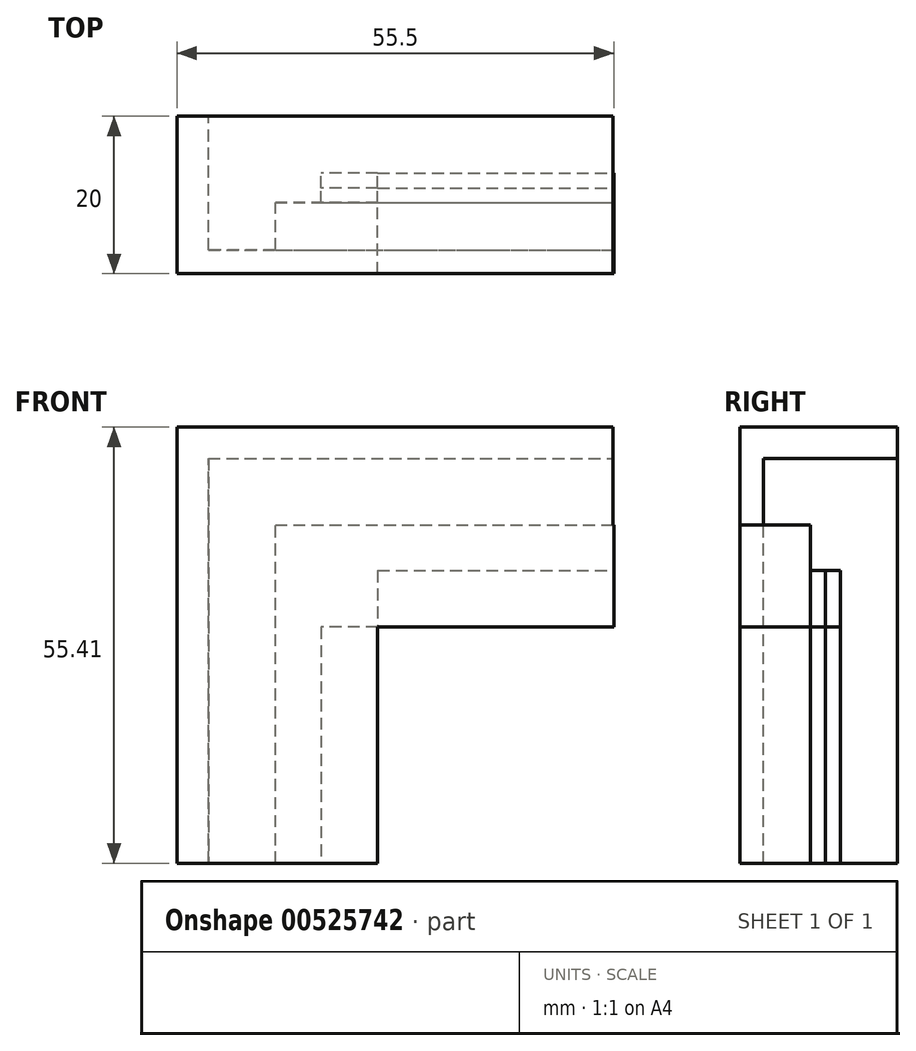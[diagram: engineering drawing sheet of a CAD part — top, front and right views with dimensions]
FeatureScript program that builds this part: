
annotation { "Feature Type Name" : "Feature", "Feature Type Description" : "" }
export const myFeature = defineFeature(function(context is Context, id is Id, definition is map)
    precondition{}
    {
        {
            var Q0;
            Q0=qCreatedBy(makeId("Front.planeOp"),FACE);
            var sketch = newSketch(context, id + "F0", { "sketchPlane" : qUnion([Q0])});
            skLineSegment(sketch, "E0.bottom", {"start": v(0, 0) * mm, "end": v(-7.2, 0) * mm});
            skLineSegment(sketch, "E0.top", {"start": v(0, -30) * mm, "end": v(-7.2, -30) * mm});
            skLineSegment(sketch, "E0.left", {"start": v(0, 0) * mm, "end": v(0, -30) * mm});
            skLineSegment(sketch, "E0.right", {"start": v(-7.2, 0) * mm, "end": v(-7.2, -30) * mm});
            skLineSegment(sketch, "E1.bottom", {"start": v(0, 0) * mm, "end": v(30, 0) * mm});
            skLineSegment(sketch, "E1.top", {"start": v(0, 7.2) * mm, "end": v(30, 7.2) * mm});
            skLineSegment(sketch, "E1.left", {"start": v(0, 0) * mm, "end": v(0, 7.2) * mm});
            skLineSegment(sketch, "E1.right", {"start": v(30, 0) * mm, "end": v(30, 7.2) * mm});
            skSolve(sketch);
        }
        {
            var Q0;
            Q0 = qSketchRegion(id + "F0", true);
            extrude(context, id + "F1", {"entities" : qUnion([Q0]), "depth" : 1.9 * mm, "offsetDistance" : 25 * mm});
        }
        {
            var Q0;
            Q0=qCreatedBy(makeId("Front.planeOp"),FACE);
            cPlane(context, id + "F2", {"entities" : qUnion([Q0]), "cplaneType" : CPlaneType.OFFSET, "offset" : 1.9 * mm, "width" : 150 * mm, "height" : 150 * mm});
        }
        {
            var Q0;
            Q0=qCreatedBy(id+"F2.planeOp",FACE);
            var sketch = newSketch(context, id + "F3", { "sketchPlane" : qUnion([Q0])});
            skLineSegment(sketch, "E2.bottom", {"start": v(0, -30) * mm, "end": v(-7.2, -30) * mm});
            skLineSegment(sketch, "E3.top", {"start": v(-7.2, 0) * mm, "end": v(30, 0) * mm});
            skLineSegment(sketch, "E3.right", {"start": v(30, 7.2) * mm, "end": v(30, 0) * mm});
            skLineSegment(sketch, "E4.top", {"start": v(-7.2, 0) * mm, "end": v(0, 0) * mm});
            skLineSegment(sketch, "E5.top", {"start": v(-7.2, -30) * mm, "end": v(0, -30) * mm});
            skLineSegment(sketch, "E5.left", {"start": v(-7.2, 0) * mm, "end": v(-7.2, -30) * mm});
            skLineSegment(sketch, "E5.right", {"start": v(0, 0) * mm, "end": v(0, -30) * mm});
            skLineSegment(sketch, "E6.bottom", {"start": v(0, 7.2) * mm, "end": v(30, 7.2) * mm});
            skLineSegment(sketch, "E6.top", {"start": v(0, 0) * mm, "end": v(30, 0) * mm});
            skLineSegment(sketch, "E6.left", {"start": v(0, 7.2) * mm, "end": v(0, 0) * mm});
            skSolve(sketch);
        }
        {
            var Q0;
            Q0=qCreatedBy(id+"F2.planeOp",FACE);
            cPlane(context, id + "F4", {"entities" : qUnion([Q0]), "cplaneType" : CPlaneType.OFFSET, "offset" : 1.9 * mm, "width" : 150 * mm, "height" : 150 * mm});
        }
        {
            var Q0;
            Q0=qCreatedBy(id+"F4.planeOp",FACE);
            var sketch = newSketch(context, id + "F5", { "sketchPlane" : qUnion([Q0])});
            skLineSegment(sketch, "E7.top", {"start": v(17.1, 0) * mm, "end": v(-12.9, 0) * mm});
            skLineSegment(sketch, "E8.bottom", {"start": v(0, -30) * mm, "end": v(-13, -30) * mm});
            skLineSegment(sketch, "E8.top", {"start": v(0, 13) * mm, "end": v(-13, 13) * mm});
            skLineSegment(sketch, "E8.left", {"start": v(0, -30) * mm, "end": v(0, 13) * mm});
            skLineSegment(sketch, "E8.right", {"start": v(-13, -30) * mm, "end": v(-13, 13) * mm});
            skLineSegment(sketch, "E9.bottom", {"start": v(-13, 13) * mm, "end": v(30, 13) * mm});
            skLineSegment(sketch, "E9.top", {"start": v(-13, 0) * mm, "end": v(30, 0) * mm});
            skLineSegment(sketch, "E9.left", {"start": v(-13, 13) * mm, "end": v(-13, 0) * mm});
            skLineSegment(sketch, "E9.right", {"start": v(30, 13) * mm, "end": v(30, 0) * mm});
            skSolve(sketch);
        }
        {
            var Q0;
            Q0 = qSketchRegion(id + "F5", true);
            extrude(context, id + "F6", {"entities" : qUnion([Q0]), "depth" : 9 * mm, "offsetDistance" : 25 * mm});
        }
        {
            var Q0;
            Q0 = qSketchRegion(id + "F3", true);
            extrude(context, id + "F7", {"entities" : qUnion([Q0]), "depth" : 1.9 * mm, "offsetDistance" : 25 * mm});
        }
        {
            var Q0;
            Q0=makeQuery(id+"F6.opExtrude","CAP_FACE",FACE,{"disambiguationData":[OSD([sQuery(id+"F5.wireOp",EDGE,"E8.bottom"),sQuery(id+"F5.wireOp",EDGE,"E8.left"),sQuery(id+"F5.wireOp",EDGE,"E8.right"),sQuery(id+"F5.wireOp",EDGE,"E9.bottom"),sQuery(id+"F5.wireOp",EDGE,"E9.top"),sQuery(id+"F5.wireOp",EDGE,"E9.left"),sQuery(id+"F5.wireOp",EDGE,"E9.right")])],"isStart":false});
            cPlane(context, id + "F8", {"entities" : qUnion([Q0]), "cplaneType" : CPlaneType.OFFSET, "offset" : 3 * mm, "oppositeDirection" : true, "width" : 150 * mm, "height" : 150 * mm});
        }
        {
            var Q0;
            Q0=qCreatedBy(id+"F8.planeOp",FACE);
            var sketch = newSketch(context, id + "F9", { "sketchPlane" : qUnion([Q0])});
            skLineSegment(sketch, "E10.bottom", {"start": v(-13, -30) * mm, "end": v(-21.5, -30) * mm});
            skLineSegment(sketch, "E10.top", {"start": v(-13, 12.9) * mm, "end": v(-21.5, 12.9) * mm});
            skLineSegment(sketch, "E10.left", {"start": v(-13, -30) * mm, "end": v(-13, 12.9) * mm});
            skLineSegment(sketch, "E10.right", {"start": v(-21.5, -30) * mm, "end": v(-21.5, 12.9) * mm});
            skLineSegment(sketch, "E11.bottom", {"start": v(-21.5, 12.9) * mm, "end": v(29.9, 12.9) * mm});
            skLineSegment(sketch, "E11.top", {"start": v(-21.5, 21.4) * mm, "end": v(29.9, 21.4) * mm});
            skLineSegment(sketch, "E11.left", {"start": v(-21.5, 12.9) * mm, "end": v(-21.5, 21.4) * mm});
            skLineSegment(sketch, "E11.right", {"start": v(29.9, 12.9) * mm, "end": v(29.9, 21.4) * mm});
            skSolve(sketch);
        }
        {
            var Q0;
            Q0 = qSketchRegion(id + "F9", true);
            extrude(context, id + "F10", {"entities" : qUnion([Q0]), "operationType" : NewBodyOperationType.ADD, "depth" : 3 * mm, "offsetDistance" : 25 * mm});
        }
        {
            var Q0;
            Q0=makeQuery(id+"F10.boolean.opBoolean","MERGE",FACE,{"derivedFrom":[makeQuery(id+"F6.opExtrude","CAP_FACE",FACE,{"disambiguationData":[OSD([sQuery(id+"F5.wireOp",EDGE,"E8.bottom"),sQuery(id+"F5.wireOp",EDGE,"E8.left"),sQuery(id+"F5.wireOp",EDGE,"E8.right"),sQuery(id+"F5.wireOp",EDGE,"E9.bottom"),sQuery(id+"F5.wireOp",EDGE,"E9.top"),sQuery(id+"F5.wireOp",EDGE,"E9.left"),sQuery(id+"F5.wireOp",EDGE,"E9.right")])],"isStart":false}),makeQuery(id+"F10.opExtrude","CAP_FACE",FACE,{"disambiguationData":[OSD([sQuery(id+"F9.wireOp",EDGE,"E10.bottom"),sQuery(id+"F9.wireOp",EDGE,"E10.left"),sQuery(id+"F9.wireOp",EDGE,"E10.right"),sQuery(id+"F9.wireOp",EDGE,"E11.bottom"),sQuery(id+"F9.wireOp",EDGE,"E11.top"),sQuery(id+"F9.wireOp",EDGE,"E11.left"),sQuery(id+"F9.wireOp",EDGE,"E11.right")])],"isStart":false})]});
            cPlane(context, id + "F11", {"entities" : qUnion([Q0]), "cplaneType" : CPlaneType.OFFSET, "offset" : 0 * mm, "width" : 150 * mm, "height" : 150 * mm});
        }
        {
            var Q0;
            Q0=qCreatedBy(id+"F11.planeOp",FACE);
            var sketch = newSketch(context, id + "F12", { "sketchPlane" : qUnion([Q0])});
            skLineSegment(sketch, "E12.bottom", {"start": v(-21.5, 21.4) * mm, "end": v(-25.5, 21.4) * mm});
            skLineSegment(sketch, "E12.top", {"start": v(-21.5, -30) * mm, "end": v(-25.5, -30) * mm});
            skLineSegment(sketch, "E12.left", {"start": v(-21.5, 21.4) * mm, "end": v(-21.5, -30) * mm});
            skLineSegment(sketch, "E12.right", {"start": v(-25.5, 21.4) * mm, "end": v(-25.5, -30) * mm});
            skLineSegment(sketch, "E13.bottom", {"start": v(-25.5, 21.4) * mm, "end": v(29.9, 21.4) * mm});
            skLineSegment(sketch, "E13.top", {"start": v(-25.5, 25.4) * mm, "end": v(29.9, 25.4) * mm});
            skLineSegment(sketch, "E13.left", {"start": v(-25.5, 21.4) * mm, "end": v(-25.5, 25.4) * mm});
            skLineSegment(sketch, "E13.right", {"start": v(29.9, 21.4) * mm, "end": v(29.9, 25.4) * mm});
            skSolve(sketch);
        }
        {
            var Q0;
            Q0 = qSketchRegion(id + "F12", true);
            extrude(context, id + "F13", {"entities" : qUnion([Q0]), "operationType" : NewBodyOperationType.ADD, "oppositeDirection" : true, "depth" : 20 * mm, "offsetDistance" : 25 * mm});
        }
    });
